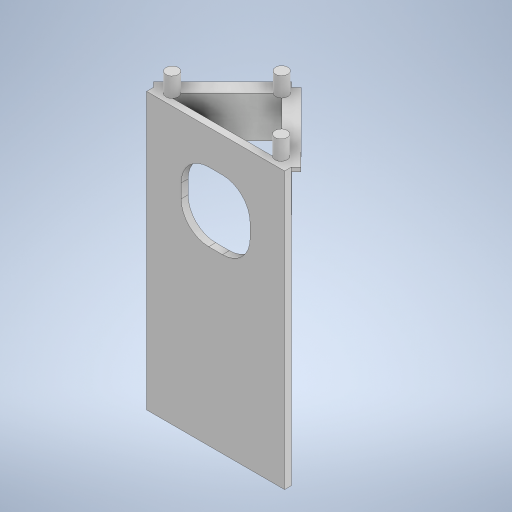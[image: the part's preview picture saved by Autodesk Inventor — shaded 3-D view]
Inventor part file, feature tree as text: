
AUTODESK INVENTOR PART (.ipt)
format: ipt  version: 2023 (Build 270158000, 158)  size: 314,368 bytes
history: native  units: mm
features: extrude x5, sketch x5
ambient origin geometry x8: Origin, YZ Plane, XZ Plane, XY Plane, X Axis, Y Axis, Z Axis, Center Point
bodies: Solid1 (feature_tree)
feature tree (10):
  extrude  "Extrusion1"  Depth=200.0mm
  extrude  "Extrusion2"  TaperAngle=45.0deg  [1 undecoded]
  extrude  "Extrusion6"  Depth=5.0mm
  extrude  "Extrusion9"  Depth=50.0mm
  extrude  "Extrusion10"  Depth=20.0mm
  sketch  "Sketch1"  dims[d0=100.0mm d1=200.0mm]
  sketch  "Sketch2"  dims[d2=5.0mm d3=0.0mm d4=45.0deg]
  sketch  "Sketch6"  dims[d5=5.0mm d6=5.0mm]
  sketch  "Sketch10"  dims[d7=30.0mm d8=0.0mm d21=50.0mm]
  sketch  "Sketch12"  dims[d22=50.0mm d23=20.0mm d24=5.0mm d25=0.0mm d33=5.0mm d34=5.0mm d36=3.0mm d37=0.0mm d38=9.0mm d39=9.0mm d41=9.0mm d42=14.0mm d43=0.0mm]
note: 1 required parameter value undecoded (feature->parameter linkage not recoverable at this tier; creation-order binding heuristic only, values carry confidence <= 0.55)
